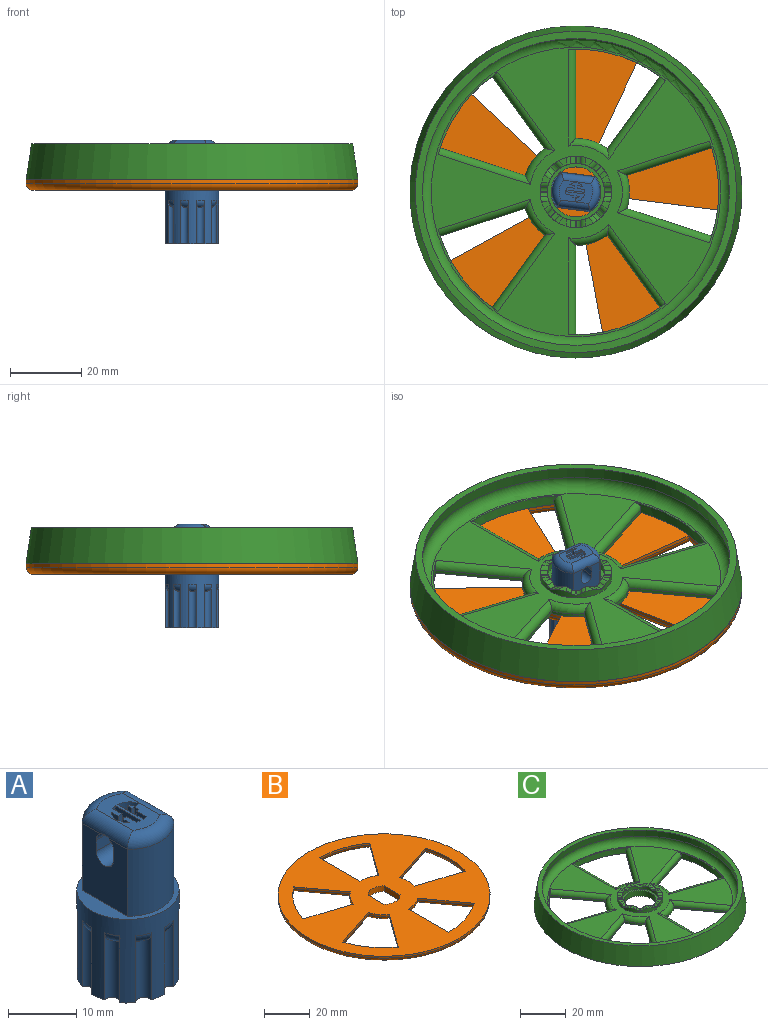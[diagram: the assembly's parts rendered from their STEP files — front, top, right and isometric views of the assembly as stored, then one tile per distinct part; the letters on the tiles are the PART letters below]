
ASSEMBLY  parts=3 mates=2
PART A: 60 faces, bbox 15.2x15.2x29 mm
  f0: plane 9.4x5.6mm, normal (0,0,1), area 36.2mm2, adj f28,f29,f30,f31,f36,f37,f38,f39
  f1: cylinder r=6.7mm len=12mm, axis (0,0,-1), area 128.4mm2, adj f2,f4,f7,f28
  f2: plane 12x9.35mm, normal (-1,0,0), area 95.9mm2, adj f1,f3,f7,f29,f32,f33,f34,f35
  f3: cylinder r=6.7mm len=12mm, axis (0,0,-1), area 128.4mm2, adj f2,f4,f7,f31
  f4: plane 12x9.35mm, normal (1,0,0), area 95.9mm2, adj f1,f3,f7,f30,f32,f33,f34,f35
  f5: cylinder r=7.5mm len=15mm, axis (0,0,1), area 424.1mm2, adj f6,f7,f8,f9,f10,f11,f12,f13
  f6: plane 15x15mm, normal (0,0,-1), area 157.5mm2, adj f5,f8,f9,f10,f11,f12,f13,f14
  f7: plane 15x15mm, normal (0,0,1), area 60.1mm2, adj f1,f2,f3,f4,f5
  f8: cylinder r=1.19mm len=12mm, axis (0,0,-1), area 35.5mm2, adj f5,f6,f27
  f9: cylinder r=1.19mm len=12mm, axis (0,0,-1), area 35.5mm2, adj f5,f6,f18
  f10: cylinder r=1.19mm len=12mm, axis (0,0,-1), area 35.5mm2, adj f5,f6,f26
  f11: cylinder r=1.19mm len=12mm, axis (0,0,-1), area 35.5mm2, adj f5,f6,f25
  f12: cylinder r=1.19mm len=12mm, axis (0,0,-1), area 35.5mm2, adj f5,f6,f24
  f13: cylinder r=1.19mm len=12mm, axis (0,0,-1), area 35.5mm2, adj f5,f6,f23
  f14: cylinder r=1.19mm len=12mm, axis (0,0,-1), area 35.5mm2, adj f5,f6,f22
  f15: cylinder r=1.19mm len=12mm, axis (0,0,-1), area 35.5mm2, adj f5,f6,f21
  f16: cylinder r=1.19mm len=12mm, axis (0,0,-1), area 35.5mm2, adj f5,f6,f20
  f17: cylinder r=1.19mm len=12mm, axis (0,0,-1), area 35.5mm2, adj f5,f6,f19
  f18: torus R=5.5mm, axis (0,0,-1), area 4.3mm2, adj f5,f9
  f19: torus R=5.5mm, axis (0,0,-1), area 4.3mm2, adj f5,f17
  f20: torus R=5.5mm, axis (0,0,-1), area 4.3mm2, adj f5,f16
  f21: torus R=5.5mm, axis (0,0,-1), area 4.3mm2, adj f5,f15
  f22: torus R=5.5mm, axis (0,0,-1), area 4.3mm2, adj f5,f14
  f23: torus R=5.5mm, axis (0,0,-1), area 4.3mm2, adj f5,f13
  f24: torus R=5.5mm, axis (0,0,-1), area 4.3mm2, adj f5,f12
  f25: torus R=5.5mm, axis (0,0,-1), area 4.3mm2, adj f5,f11
  f26: torus R=5.5mm, axis (0,0,-1), area 4.3mm2, adj f5,f10
  f27: torus R=5.5mm, axis (0,0,-1), area 4.3mm2, adj f5,f8
  f28: torus R=4.7mm, axis (0,0,1), area 28.2mm2, adj f0,f1,f29,f30
  f29: cylinder r=2mm len=9.35mm, axis (0,1,0), area 27.1mm2, adj f0,f2,f28,f31,f35
  f30: cylinder r=2mm len=9.35mm, axis (0,-1,0), area 27.1mm2, adj f0,f4,f28,f31,f35
  f31: torus R=4.7mm, axis (0,0,1), area 28.2mm2, adj f0,f3,f29,f30
  f32: plane 9.6x2mm, normal (0,1,0), area 19.2mm2, adj f2,f4,f33,f35
  f33: cylinder r=1.75mm len=9.6mm, axis (1,0,0), area 52.8mm2, adj f2,f4,f32,f34
  f34: plane 9.6x2mm, normal (0,-1,0), area 19.2mm2, adj f2,f4,f33,f35
  f35: cylinder r=1.75mm len=9.6mm, axis (1,0,0), area 52.8mm2, adj f2,f4,f29,f30,f32,f34
  f36: plane 1.2x0.46mm, normal (0,1,0), area 0.5mm2, adj f0,f37,f46,f47
  f37: plane 1.2x0.92mm, normal (-1,0,0), area 1.1mm2, adj f0,f36,f38,f47
  f38: plane 1.2x0.46mm, normal (0,-1,0), area 0.5mm2, adj f0,f37,f39,f47
  f39: plane 1.2x0.97mm, normal (-1,0,0), area 1.2mm2, adj f0,f38,f40,f47
  f40: plane 1.2x0.01mm, normal (0.47,0.88,0), area 0mm2, adj f0,f39,f41,f47
  f41: cylinder r=1.76mm len=1.2mm, axis (0,0,1), area 1.5mm2, adj f0,f40,f42,f47
  f42: plane 1.2x0.87mm, normal (-0.22,0.98,0), area 1.1mm2, adj f0,f41,f43,f47
  f43: cylinder r=2.65mm len=2.36mm, axis (0,0,1), area 4mm2, adj f0,f42,f44,f47
  f44: plane 5.29x1.2mm, normal (1,0,0), area 6.3mm2, adj f0,f43,f45,f47
  f45: cylinder r=2.65mm len=1.2mm, axis (0,0,1), area 1mm2, adj f0,f44,f46,f47
  f46: plane 1.99x1.2mm, normal (-1,0,0), area 2.4mm2, adj f0,f36,f45,f47
  f47: plane 5.29x2.36mm, normal (0,0,1), area 6.2mm2, adj f36,f37,f38,f39,f40,f41,f42,f43
  f48: cylinder r=2.65mm len=1.2mm, axis (0,0,1), area 1mm2, adj f0,f49,f58,f59
  f49: plane 5.29x1.2mm, normal (-1,0,0), area 6.3mm2, adj f0,f48,f50,f59
  f50: cylinder r=2.65mm len=1.2mm, axis (0,0,1), area 1mm2, adj f0,f49,f51,f59
  f51: plane 1.99x1.2mm, normal (1,0,0), area 2.4mm2, adj f0,f50,f52,f59
  f52: plane 1.2x0.8mm, normal (0,-1,0), area 1mm2, adj f0,f51,f53,f59
  f53: plane 1.43x1.2mm, normal (-1,0,0), area 1.7mm2, adj f0,f52,f54,f59
  f54: cylinder r=2.63mm len=3.78mm, axis (0,0,1), area 5.1mm2, adj f0,f53,f55,f59
  f55: plane 1.43x1.2mm, normal (-1,0,0), area 1.7mm2, adj f0,f54,f56,f59
  f56: plane 1.2x0.8mm, normal (0,1,0), area 1mm2, adj f0,f55,f57,f59
  f57: plane 1.99x1.2mm, normal (1,0,0), area 2.4mm2, adj f0,f56,f58,f59
  f58: plane 1.2x0mm, normal (1,0.01,0), area 0mm2, adj f0,f48,f57,f59
  f59: plane 5.29x2.4mm, normal (0,0,1), area 6.9mm2, adj f48,f49,f50,f51,f52,f53,f54,f55
PART B: 48 faces, bbox 100.7x100.7x3.4 mm
  f0: cylinder r=7mm len=10mm, axis (0,0,1), area 33.4mm2, adj f2,f3,f46,f47
  f1: cylinder r=7mm len=10mm, axis (0,0,1), area 33.4mm2, adj f2,f3,f46,f47
  f2: plane 93x93mm, normal (0,0,1), area 4506.1mm2, adj f0,f1,f4,f5,f6,f7,f8,f9
  f3: plane 89x89mm, normal (0,0,-1), area 3008mm2, adj f0,f1,f25,f26,f27,f28,f29,f30
  f4: cylinder r=46.5mm len=93mm, axis (0,0,1), area 292.2mm2, adj f2,f45
  f5: plane 25x1mm, normal (1,0,0), area 25mm2, adj f2,f6,f8,f44
  f6: cylinder r=15mm len=8.82mm, axis (0,0,1), area 9.4mm2, adj f2,f5,f7,f42
  f7: plane 20.23x14.69mm, normal (-0.81,0.59,0), area 25mm2, adj f2,f6,f8,f41
  f8: cylinder r=40mm len=23.51mm, axis (0,0,1), area 25.1mm2, adj f2,f5,f7,f43
  f9: cylinder r=15mm len=8.82mm, axis (0,0,1), area 9.4mm2, adj f2,f10,f12,f40
  f10: plane 25x1mm, normal (1,0,0), area 25mm2, adj f2,f9,f11,f38
  f11: cylinder r=40mm len=23.51mm, axis (0,0,1), area 25.1mm2, adj f2,f10,f12,f37
  f12: plane 20.23x14.69mm, normal (-0.81,-0.59,0), area 25mm2, adj f2,f9,f11,f39
  f13: plane 23.78x7.73mm, normal (0.31,-0.95,0), area 25mm2, adj f2,f14,f16,f36
  f14: cylinder r=15mm len=9.27mm, axis (0,0,1), area 9.4mm2, adj f2,f13,f15,f34
  f15: plane 23.78x7.73mm, normal (0.31,0.95,0), area 25mm2, adj f2,f14,f16,f33
  f16: cylinder r=40mm len=24.72mm, axis (0,0,1), area 25.1mm2, adj f2,f13,f15,f35
  f17: cylinder r=15mm len=7.5mm, axis (0,0,1), area 9.4mm2, adj f2,f18,f20,f32
  f18: plane 23.78x7.73mm, normal (0.31,-0.95,0), area 25mm2, adj f2,f17,f19,f30
  f19: cylinder r=40mm len=20mm, axis (0,0,1), area 25.1mm2, adj f2,f18,f20,f29
  f20: plane 20.23x14.69mm, normal (-0.81,0.59,0), area 25mm2, adj f2,f17,f19,f31
  f21: cylinder r=15mm len=7.5mm, axis (0,0,1), area 9.4mm2, adj f2,f22,f24,f28
  f22: plane 20.23x14.69mm, normal (-0.81,-0.59,0), area 25mm2, adj f2,f21,f23,f26
  f23: cylinder r=40mm len=20mm, axis (0,0,1), area 25.1mm2, adj f2,f22,f24,f25
  f24: plane 23.78x7.73mm, normal (0.31,0.95,0), area 25mm2, adj f2,f21,f23,f27
  f25: torus R=42mm, axis (0,0,1), area 85mm2, adj f3,f23,f26,f27
  f26: cylinder r=2mm len=24.72mm, axis (-0.59,0.81,0), area 83.2mm2, adj f3,f22,f25,f28
  f27: cylinder r=2mm len=28.3mm, axis (0.95,-0.31,0), area 83.2mm2, adj f3,f24,f25,f28
  f28: torus R=13mm, axis (0,0,1), area 32.7mm2, adj f3,f21,f26,f27
  f29: torus R=42mm, axis (0,0,1), area 85mm2, adj f3,f19,f30,f31
  f30: cylinder r=2mm len=28.3mm, axis (-0.95,-0.31,0), area 83.2mm2, adj f3,f18,f29,f32
  f31: cylinder r=2mm len=24.72mm, axis (0.59,0.81,0), area 83.2mm2, adj f3,f20,f29,f32
  f32: torus R=13mm, axis (0,0,1), area 32.7mm2, adj f3,f17,f30,f31
  f33: cylinder r=2mm len=28.3mm, axis (0.95,-0.31,0), area 83.2mm2, adj f3,f15,f34,f35
  f34: torus R=13mm, axis (0,0,1), area 32.7mm2, adj f3,f14,f33,f36
  f35: torus R=42mm, axis (0,0,1), area 85mm2, adj f3,f16,f33,f36
  f36: cylinder r=2mm len=28.3mm, axis (-0.95,-0.31,0), area 83.2mm2, adj f3,f13,f34,f35
  f37: torus R=42mm, axis (0,0,1), area 85mm2, adj f3,f11,f38,f39
  f38: cylinder r=2mm len=29.11mm, axis (0,-1,0), area 83.2mm2, adj f3,f10,f37,f40
  f39: cylinder r=2mm len=24.72mm, axis (-0.59,0.81,0), area 83.2mm2, adj f3,f12,f37,f40
  f40: torus R=13mm, axis (0,0,1), area 32.7mm2, adj f3,f9,f38,f39
  f41: cylinder r=2mm len=24.72mm, axis (0.59,0.81,0), area 83.2mm2, adj f3,f7,f42,f43
  f42: torus R=13mm, axis (0,0,1), area 32.7mm2, adj f3,f6,f41,f44
  f43: torus R=42mm, axis (0,0,1), area 85mm2, adj f3,f8,f41,f44
  f44: cylinder r=2mm len=29.11mm, axis (0,-1,0), area 83.2mm2, adj f3,f5,f42,f43
  f45: torus R=44.5mm, axis (0,0,1), area 903.5mm2, adj f3,f4
  f46: plane 9.8x3mm, normal (1,0,0), area 29.4mm2, adj f0,f1,f2,f3
  f47: plane 9.8x3mm, normal (-1,0,0), area 29.4mm2, adj f0,f1,f2,f3
PART C: 93 faces, bbox 94.3x94.3x10 mm
  f0: plane 2x0.17mm, normal (0,0,1), area 0.3mm2, adj f51,f52,f77,f90
  f1: plane 1.54x1.54mm, normal (0,0,1), area 0.3mm2, adj f51,f52,f78,f79
  f2: plane 2x0.17mm, normal (0,0,1), area 0.3mm2, adj f51,f52,f80,f81
  f3: plane 1.54x1.54mm, normal (0,0,1), area 0.3mm2, adj f51,f52,f82,f84
  f4: plane 2x0.17mm, normal (0,0,1), area 0.3mm2, adj f51,f52,f83,f86
  f5: plane 1.54x1.54mm, normal (0,0,1), area 0.3mm2, adj f51,f52,f85,f88
  f6: plane 2x0.17mm, normal (0,0,1), area 0.3mm2, adj f51,f52,f87,f92
  f7: plane 1.54x1.54mm, normal (0,0,1), area 0.3mm2, adj f51,f52,f89,f91
  f8: plane 16x16mm, normal (0,0,1), area 47.1mm2, adj f12,f51
  f9: plane 81.09x81.09mm, normal (0,0,1), area 2061.6mm2, adj f18,f21,f26,f29,f33,f35,f36,f37
  f10: plane 93x93mm, normal (0,0,-1), area 4479.1mm2, adj f12,f13,f15,f16,f17,f18,f19,f20
  f11: cone r=44.03mm half-angle=8.5deg, axis (0,0,-1), area 976.7mm2, adj f14,f35
  f12: cylinder r=7mm len=14mm, axis (0,0,1), area 131.9mm2, adj f8,f10
  f13: cone r=46.5mm half-angle=8.5deg, axis (0,0,-1), area 2906.7mm2, adj f10,f14
  f14: plane 90x90mm, normal (0,0,1), area 559mm2, adj f11,f13
  f15: plane 25x1mm, normal (1,0,0), area 25mm2, adj f10,f16,f18,f49
  f16: cylinder r=15mm len=8.82mm, axis (0,0,1), area 9.4mm2, adj f10,f15,f17,f50
  f17: plane 20.23x14.69mm, normal (-0.81,0.59,0), area 25mm2, adj f10,f16,f18,f48
  f18: cylinder r=40mm len=27.1mm, axis (0,0,1), area 77.1mm2, adj f9,f10,f15,f17,f48,f49
  f19: cylinder r=15mm len=8.82mm, axis (0,0,1), area 9.4mm2, adj f10,f20,f22,f43
  f20: plane 25x1mm, normal (1,0,0), area 25mm2, adj f10,f19,f21,f44
  f21: cylinder r=40mm len=27.1mm, axis (0,0,1), area 77.1mm2, adj f9,f10,f20,f22,f42,f44
  f22: plane 20.23x14.69mm, normal (-0.81,-0.59,0), area 25mm2, adj f10,f19,f21,f42
  f23: plane 23.78x7.73mm, normal (0.31,-0.95,0), area 25mm2, adj f10,f24,f26,f45
  f24: cylinder r=15mm len=9.27mm, axis (0,0,1), area 9.4mm2, adj f10,f23,f25,f46
  f25: plane 23.78x7.73mm, normal (0.31,0.95,0), area 25mm2, adj f10,f24,f26,f47
  f26: cylinder r=40mm len=28.49mm, axis (0,0,1), area 77.1mm2, adj f9,f10,f23,f25,f45,f47
  f27: cylinder r=15mm len=7.5mm, axis (0,0,1), area 9.4mm2, adj f10,f28,f30,f40
  f28: plane 23.78x7.73mm, normal (0.31,-0.95,0), area 25mm2, adj f10,f27,f29,f41
  f29: cylinder r=40mm len=23.05mm, axis (0,0,1), area 77.1mm2, adj f9,f10,f28,f30,f39,f41
  f30: plane 20.23x14.69mm, normal (-0.81,0.59,0), area 25mm2, adj f10,f27,f29,f39
  f31: cylinder r=15mm len=7.5mm, axis (0,0,1), area 9.4mm2, adj f10,f32,f34,f37
  f32: plane 20.23x14.69mm, normal (-0.81,-0.59,0), area 25mm2, adj f10,f31,f33,f38
  f33: cylinder r=40mm len=23.05mm, axis (0,0,1), area 77.1mm2, adj f9,f10,f32,f34,f36,f38
  f34: plane 23.78x7.73mm, normal (0.31,0.95,0), area 25mm2, adj f10,f31,f33,f36
  f35: torus R=40.54mm, axis (0,0,1), area 1379.2mm2, adj f9,f11
  f36: cylinder r=2mm len=26.44mm, axis (-0.95,0.31,0), area 80.9mm2, adj f9,f33,f34,f37
  f37: torus R=13mm, axis (0,0,1), area 32.7mm2, adj f9,f31,f36,f38
  f38: cylinder r=2mm len=23.14mm, axis (0.59,-0.81,0), area 80.9mm2, adj f9,f32,f33,f37
  f39: cylinder r=2mm len=23.14mm, axis (-0.59,-0.81,0), area 80.9mm2, adj f9,f29,f30,f40
  f40: torus R=13mm, axis (0,0,1), area 32.7mm2, adj f9,f27,f39,f41
  f41: cylinder r=2mm len=26.44mm, axis (0.95,0.31,0), area 80.9mm2, adj f9,f28,f29,f40
  f42: cylinder r=2mm len=23.14mm, axis (0.59,-0.81,0), area 80.9mm2, adj f9,f21,f22,f43
  f43: torus R=13mm, axis (0,0,1), area 32.7mm2, adj f9,f19,f42,f44
  f44: cylinder r=2mm len=27.15mm, axis (0,1,0), area 80.9mm2, adj f9,f20,f21,f43
  f45: cylinder r=2mm len=26.44mm, axis (0.95,0.31,0), area 80.9mm2, adj f9,f23,f26,f46
  f46: torus R=13mm, axis (0,0,1), area 32.7mm2, adj f9,f24,f45,f47
  f47: cylinder r=2mm len=26.44mm, axis (-0.95,0.31,0), area 80.9mm2, adj f9,f25,f26,f46
  f48: cylinder r=2mm len=23.14mm, axis (-0.59,-0.81,0), area 80.9mm2, adj f9,f17,f18,f50
  f49: cylinder r=2mm len=27.15mm, axis (0,1,0), area 80.9mm2, adj f9,f15,f18,f50
  f50: torus R=13mm, axis (0,0,1), area 32.7mm2, adj f9,f16,f48,f49
  f51: cylinder r=8mm len=16mm, axis (0,0,-1), area 77.8mm2, adj f0,f1,f2,f3,f4,f5,f6,f7
  f52: cylinder r=10mm len=20mm, axis (0,0,-1), area 103mm2, adj f0,f1,f2,f3,f4,f5,f6,f7
  f53: plane 2.37x2.14mm, normal (0,0,1), area 3mm2, adj f51,f52,f73,f74
  f54: plane 2.37x2.14mm, normal (0,0,1), area 3mm2, adj f51,f52,f75,f76
  f55: plane 2.37x2.14mm, normal (0,0,1), area 3mm2, adj f51,f52,f71,f72
  f56: plane 2.37x2.14mm, normal (0,0,1), area 3mm2, adj f51,f52,f69,f70
  f57: plane 2.37x2.14mm, normal (0,0,1), area 3mm2, adj f51,f52,f67,f68
  f58: plane 2.37x2.14mm, normal (0,0,1), area 3mm2, adj f51,f52,f65,f66
  f59: plane 2.37x2.14mm, normal (0,0,1), area 3mm2, adj f51,f52,f63,f64
  f60: plane 2.37x2.14mm, normal (0,0,1), area 3mm2, adj f51,f52,f61,f62
  f61: cylinder r=2mm len=2.38mm, axis (-1,0,0), area 2.9mm2, adj f51,f52,f60,f77
  f62: cylinder r=2mm len=2.62mm, axis (-0.71,0.71,0), area 2.9mm2, adj f51,f52,f60,f78
  f63: cylinder r=2mm len=2.62mm, axis (-0.71,0.71,0), area 2.9mm2, adj f51,f52,f59,f79
  f64: cylinder r=2mm len=2.38mm, axis (0,1,0), area 2.9mm2, adj f51,f52,f59,f80
  f65: cylinder r=2mm len=2.38mm, axis (0,1,0), area 2.9mm2, adj f51,f52,f58,f81
  f66: cylinder r=2mm len=2.62mm, axis (0.71,0.71,0), area 2.9mm2, adj f51,f52,f58,f82
  f67: cylinder r=2mm len=2.38mm, axis (-1,0,0), area 2.9mm2, adj f51,f52,f57,f83
  f68: cylinder r=2mm len=2.62mm, axis (0.71,0.71,0), area 2.9mm2, adj f51,f52,f57,f84
  f69: cylinder r=2mm len=2.62mm, axis (-0.71,0.71,0), area 2.9mm2, adj f51,f52,f56,f85
  f70: cylinder r=2mm len=2.38mm, axis (-1,0,0), area 2.9mm2, adj f51,f52,f56,f86
  f71: cylinder r=2mm len=2.38mm, axis (0,1,0), area 2.9mm2, adj f51,f52,f55,f87
  f72: cylinder r=2mm len=2.62mm, axis (-0.71,0.71,0), area 2.9mm2, adj f51,f52,f55,f88
  f73: cylinder r=2mm len=2.62mm, axis (0.71,0.71,0), area 2.9mm2, adj f51,f52,f53,f89
  f74: cylinder r=2mm len=2.38mm, axis (-1,0,0), area 2.9mm2, adj f51,f52,f53,f90
  f75: cylinder r=2mm len=2.62mm, axis (0.71,0.71,0), area 2.9mm2, adj f51,f52,f54,f91
  f76: cylinder r=2mm len=2.38mm, axis (0,1,0), area 2.9mm2, adj f51,f52,f54,f92
  f77: cylinder r=2mm len=2.12mm, axis (-1,0,0), area 2.9mm2, adj f0,f51,f52,f61
  f78: cylinder r=2mm len=2.44mm, axis (-0.71,0.71,0), area 2.9mm2, adj f1,f51,f52,f62
  f79: cylinder r=2mm len=2.44mm, axis (-0.71,0.71,0), area 2.9mm2, adj f1,f51,f52,f63
  f80: cylinder r=2mm len=2.12mm, axis (0,1,0), area 2.9mm2, adj f2,f51,f52,f64
  f81: cylinder r=2mm len=2.12mm, axis (0,1,0), area 2.9mm2, adj f2,f51,f52,f65
  f82: cylinder r=2mm len=2.44mm, axis (0.71,0.71,0), area 2.9mm2, adj f3,f51,f52,f66
  f83: cylinder r=2mm len=2.12mm, axis (-1,0,0), area 2.9mm2, adj f4,f51,f52,f67
  f84: cylinder r=2mm len=2.44mm, axis (0.71,0.71,0), area 2.9mm2, adj f3,f51,f52,f68
  f85: cylinder r=2mm len=2.44mm, axis (-0.71,0.71,0), area 2.9mm2, adj f5,f51,f52,f69
  f86: cylinder r=2mm len=2.12mm, axis (-1,0,0), area 2.9mm2, adj f4,f51,f52,f70
  f87: cylinder r=2mm len=2.12mm, axis (0,1,0), area 2.9mm2, adj f6,f51,f52,f71
  f88: cylinder r=2mm len=2.44mm, axis (-0.71,0.71,0), area 2.9mm2, adj f5,f51,f52,f72
  f89: cylinder r=2mm len=2.44mm, axis (0.71,0.71,0), area 2.9mm2, adj f7,f51,f52,f73
  f90: cylinder r=2mm len=2.12mm, axis (-1,0,0), area 2.9mm2, adj f0,f51,f52,f74
  f91: cylinder r=2mm len=2.44mm, axis (0.71,0.71,0), area 2.9mm2, adj f7,f51,f52,f75
  f92: cylinder r=2mm len=2.12mm, axis (0,1,0), area 2.9mm2, adj f6,f51,f52,f76
PLACE A rot(axis=(0,0,-1),97.3deg) t=(16.69,15.36,-163.7)mm
PLACE B rot(axis=(0,0,-1),97.3deg) t=(16.69,15.36,-160.7)mm
PLACE C t=(16.69,15.36,-157.7)mm
MATE fastened B.f0 <-> A.f5  axis (0,0,-1) through (16.69,15.36,-160.7)mm
MATE revolute C.f11 <-> B.f23  axis (0,0,-1) through (16.69,15.36,-157.7)mm
